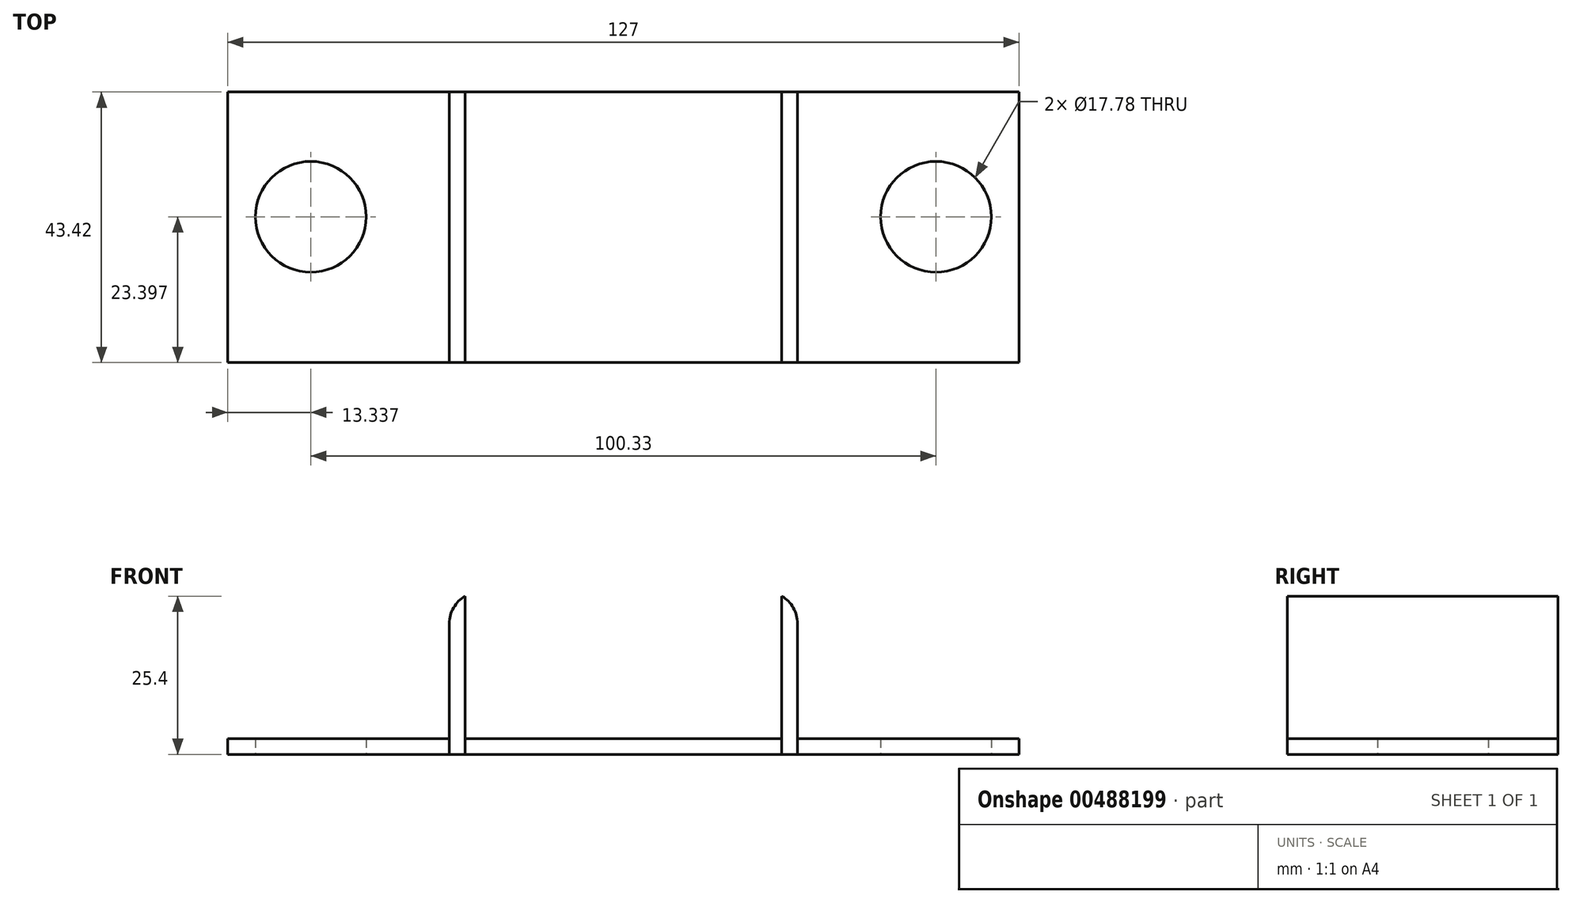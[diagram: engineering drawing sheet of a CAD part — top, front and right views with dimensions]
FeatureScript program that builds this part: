
annotation { "Feature Type Name" : "Feature", "Feature Type Description" : "" }
export const myFeature = defineFeature(function(context is Context, id is Id, definition is map)
    precondition{}
    {
        {
            var Q0;
            Q0=qCreatedBy(makeId("Top.planeOp"),FACE);
            var sketch = newSketch(context, id + "F0", { "sketchPlane" : qUnion([Q0])});
            skLineSegment(sketch, "E0.bottom", {"start": v(94.52, -71.05) * mm, "end": v(-32.48, -71.05) * mm});
            skLineSegment(sketch, "E0.top", {"start": v(94.52, -27.63) * mm, "end": v(-32.48, -27.63) * mm});
            skLineSegment(sketch, "E0.left", {"start": v(94.52, -71.05) * mm, "end": v(94.52, -27.63) * mm});
            skLineSegment(sketch, "E0.right", {"start": v(-32.48, -71.05) * mm, "end": v(-32.48, -27.63) * mm});
            skPoint(sketch, "E0.middle", {"position": v(31.02, -49.34) * mm});
            skCircle(sketch, "E1.cCircle", {"center": v(-19.14, -47.65) * mm, "radius": 6.35 * mm, "construction": true});
            skLineSegment(sketch, "E1.0", {"start": v(-12.8, -43.99) * mm, "end": v(-12.8, -51.32) * mm});
            skLineSegment(sketch, "E1.1", {"start": v(-12.8, -51.32) * mm, "end": v(-19.14, -54.99) * mm});
            skLineSegment(sketch, "E1.2", {"start": v(-19.14, -54.99) * mm, "end": v(-25.5, -51.32) * mm});
            skLineSegment(sketch, "E1.3", {"start": v(-25.5, -51.32) * mm, "end": v(-25.5, -43.99) * mm});
            skLineSegment(sketch, "E1.4", {"start": v(-25.5, -43.99) * mm, "end": v(-19.14, -40.32) * mm});
            skLineSegment(sketch, "E1.5", {"start": v(-19.14, -40.32) * mm, "end": v(-12.8, -43.99) * mm});
            skPoint(sketch, "E1.0.midPoint", {"position": v(-12.8, -47.65) * mm});
            skCircle(sketch, "E2.cCircle", {"center": v(81.19, -47.65) * mm, "radius": 6.35 * mm, "construction": true});
            skLineSegment(sketch, "E2.0", {"start": v(78.57, -54.5) * mm, "end": v(73.95, -48.8) * mm});
            skLineSegment(sketch, "E2.1", {"start": v(73.95, -48.8) * mm, "end": v(76.57, -41.96) * mm});
            skLineSegment(sketch, "E2.2", {"start": v(76.57, -41.96) * mm, "end": v(83.8, -40.8) * mm});
            skLineSegment(sketch, "E2.3", {"start": v(83.8, -40.8) * mm, "end": v(88.43, -46.5) * mm});
            skLineSegment(sketch, "E2.4", {"start": v(88.43, -46.5) * mm, "end": v(85.8, -53.35) * mm});
            skLineSegment(sketch, "E2.5", {"start": v(85.8, -53.35) * mm, "end": v(78.57, -54.5) * mm});
            skPoint(sketch, "E2.0.midPoint", {"position": v(76.26, -51.65) * mm});
            skLineSegment(sketch, "E3", {"start": v(5.62, -27.63) * mm, "end": v(5.62, -71.05) * mm});
            skLineSegment(sketch, "E4", {"start": v(56.42, -27.63) * mm, "end": v(56.42, -71.05) * mm});
            skLineSegment(sketch, "E5", {"start": v(3.08, -27.63) * mm, "end": v(3.08, -71.05) * mm});
            skLineSegment(sketch, "E6", {"start": v(58.96, -27.63) * mm, "end": v(58.96, -71.05) * mm});
            skCircle(sketch, "E7", {"center": v(-19.14, -47.65) * mm, "radius": 8.9 * mm});
            skCircle(sketch, "E8", {"center": v(81.19, -47.65) * mm, "radius": 8.9 * mm});
            skSolve(sketch);
        }
        {
            var Q0;
            {var subQ0=sQuery(id+"F0.wireOp",EDGE,"E3");Q0=makeQuery(id+"F0.imprint","IMPRINT",FACE,{"disambiguationData":[TD([[makeQuery(id+"F0.imprint","IMPRINT",EDGE,{"derivedFrom":subQ0}),-1.0]])]});}
            var Q1;
            {var subQ0=sQuery(id+"F0.wireOp",EDGE,"E4");Q1=makeQuery(id+"F0.imprint","IMPRINT",FACE,{"disambiguationData":[TD([[makeQuery(id+"F0.imprint","IMPRINT",EDGE,{"derivedFrom":subQ0}),1.0]])]});}
            extrude(context, id + "F1", {"entities" : qUnion([Q0, Q1]), "depth" : 25.4 * mm});
        }
        {
            var Q0;
            {var subQ1=sQuery(id+"F0.wireOp",EDGE,"E0.right");Q0=makeQuery(id+"F0.imprint","IMPRINT",FACE,{"disambiguationData":[TD([[makeQuery(id+"F0.imprint","IMPRINT",EDGE,{"derivedFrom":subQ1}),-1.0]])]});}
            var Q1;
            {var subQ0=sQuery(id+"F0.wireOp",EDGE,"E3");Q1=makeQuery(id+"F0.imprint","IMPRINT",FACE,{"disambiguationData":[TD([[makeQuery(id+"F0.imprint","IMPRINT",EDGE,{"derivedFrom":subQ0}),1.0]])]});}
            var Q2;
            {var subQ1=sQuery(id+"F0.wireOp",EDGE,"E0.left");Q2=makeQuery(id+"F0.imprint","IMPRINT",FACE,{"disambiguationData":[TD([[makeQuery(id+"F0.imprint","IMPRINT",EDGE,{"derivedFrom":subQ1}),1.0]])]});}
            extrude(context, id + "F2", {"entities" : qUnion([Q0, Q1, Q2]), "depth" : 2.54 * mm});
        }
        {
            var Q0;
            Q0=makeQuery(id+"F1.opExtrude","CAP_EDGE",EDGE,{"disambiguationData":[OSD([sQuery(id+"F0.wireOp",EDGE,"E5")])],"isStart":false});
            var Q1;
            Q1=makeQuery(id+"F1.opExtrude","CAP_EDGE",EDGE,{"disambiguationData":[OSD([sQuery(id+"F0.wireOp",EDGE,"E6")])],"isStart":false});
            fillet(context, id + "F3", {"entities" : qUnion([Q0, Q1]), "radius" : 5.08 * mm, "tangentPropagation" : true, "allowEdgeOverflow" : false});
        }
    });
